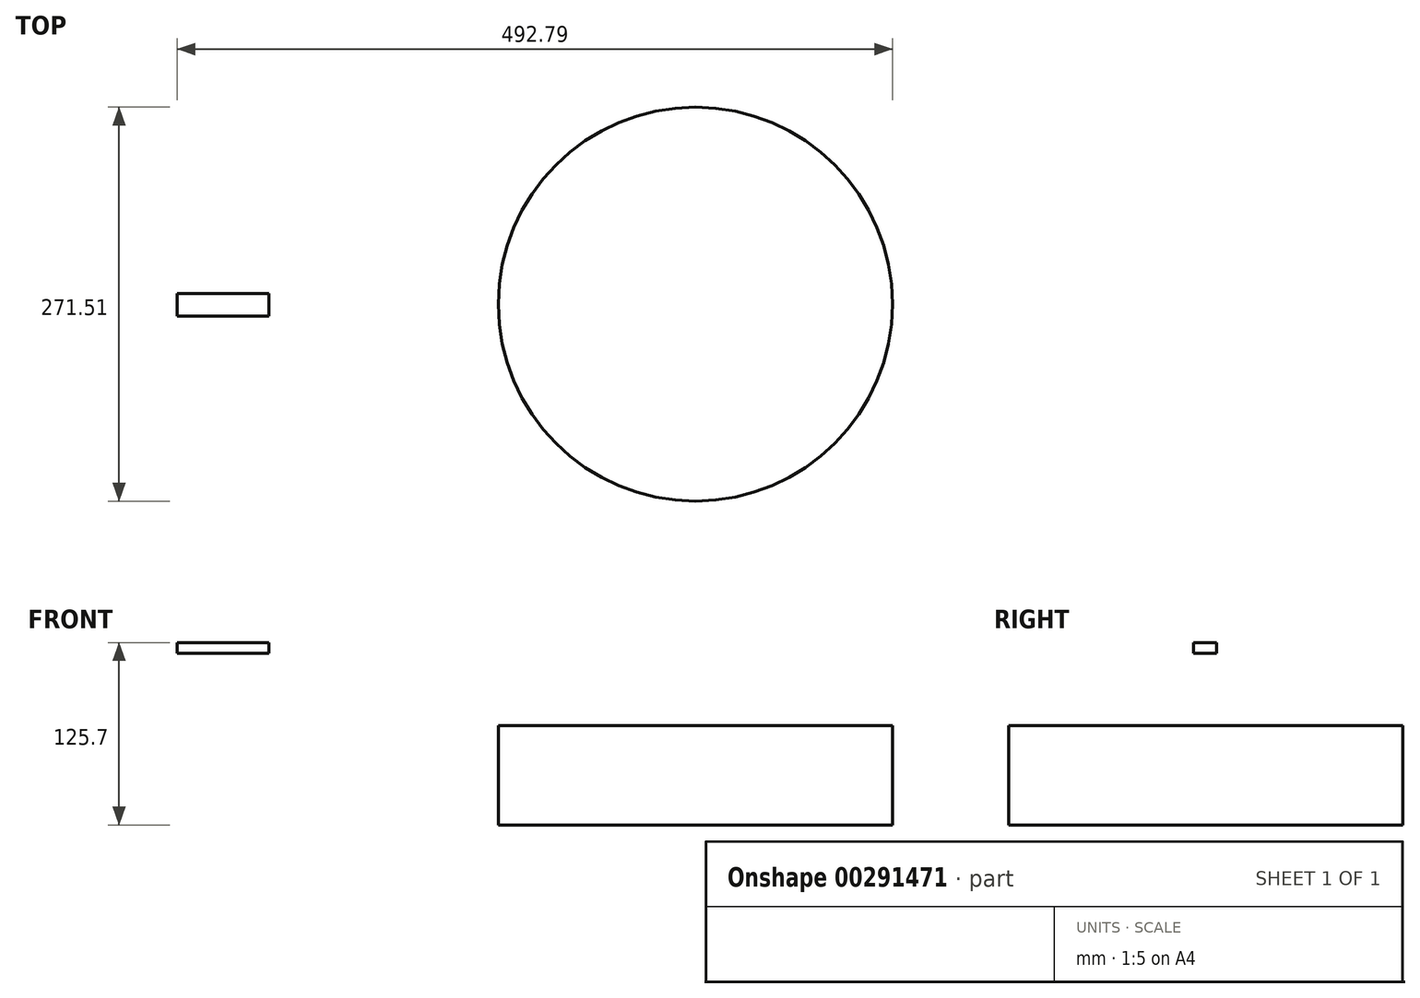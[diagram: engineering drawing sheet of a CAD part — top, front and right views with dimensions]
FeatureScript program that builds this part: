
annotation { "Feature Type Name" : "Feature", "Feature Type Description" : "" }
export const myFeature = defineFeature(function(context is Context, id is Id, definition is map)
    precondition{}
    {
        {
            var Q0;
            Q0=qCreatedBy(makeId("Front.planeOp"),FACE);
            var sketch = newSketch(context, id + "F0", { "sketchPlane" : qUnion([Q0])});
            skSolve(sketch);
        }
        {
            var Q0;
            Q0=qCreatedBy(makeId("Top.planeOp"),FACE);
            var sketch = newSketch(context, id + "F1", { "sketchPlane" : qUnion([Q0])});
            skCircle(sketch, "E0", {"center": v(0, 0) * mm, "radius": 8.39 * mm});
            skSolve(sketch);
        }
        {
            var Q0;
            Q0=makeQuery(id+"F1.imprint","IMPRINT",FACE,{"disambiguationData":[TD([[makeQuery(id+"F1.imprint","IMPRINT",EDGE,{"derivedFrom":sQuery(id+"F1.wireOp",EDGE,"E0")}),1.0]])]});
            var Q1;
            Q1=sQuery(id+"F1.wireOp",EDGE,"E0");
            var Q2;
            Q2 = qConstructionFilter(qBodyType(qCreatedBy(id + "F0" ,EDGE), BodyType.WIRE), ConstructionObject.NO);
            extrude(context, id + "F2", {"entities" : qUnion([Q0]), "bodyType" : ToolBodyType.SURFACE, "surfaceEntities" : qUnion([Q1, Q2]), "endBound" : BoundingType.SYMMETRIC, "depth" : 95 * mm, "offsetDistance" : 25.4 * mm});
        }
        {
            var Q0;
            Q0=qCreatedBy(makeId("Front.planeOp"),FACE);
            var sketch = newSketch(context, id + "F3", { "sketchPlane" : qUnion([Q0])});
            skLineSegment(sketch, "E1.bottom", {"start": v(-71.58, 57.12) * mm, "end": v(-8.49, 57.12) * mm});
            skLineSegment(sketch, "E1.top", {"start": v(-71.58, 49.67) * mm, "end": v(-8.49, 49.67) * mm});
            skLineSegment(sketch, "E1.left", {"start": v(-71.58, 57.12) * mm, "end": v(-71.58, 49.67) * mm});
            skLineSegment(sketch, "E1.right", {"start": v(-8.49, 57.12) * mm, "end": v(-8.49, 49.67) * mm});
            skSolve(sketch);
        }
        {
            var Q0;
            Q0=makeQuery(id+"F3.imprint","IMPRINT",FACE,{"disambiguationData":[TD([[makeQuery(id+"F3.imprint","IMPRINT",EDGE,{"derivedFrom":sQuery(id+"F3.wireOp",EDGE,"E1.bottom")}),-1.0]])]});
            extrude(context, id + "F4", {"entities" : qUnion([Q0]), "endBound" : BoundingType.SYMMETRIC, "depth" : 15.75 * mm, "offsetDistance" : 25.4 * mm});
        }
        {
            var Q0;
            Q0=qCreatedBy(makeId("Right.planeOp"),FACE);
            var sketch = newSketch(context, id + "F5", { "sketchPlane" : qUnion([Q0])});
            skCircle(sketch, "E2", {"center": v(0, 26.45) * mm, "radius": 7.62 * mm});
            skSolve(sketch);
        }
        {
            var Q0;
            Q0 = qSketchRegion(id + "F5", true);
            var Q1;
            Q1=sQuery(id+"F5.wireOp",EDGE,"E2");
            extrude(context, id + "F6", {"entities" : qUnion([Q0]), "bodyType" : ToolBodyType.SURFACE, "surfaceEntities" : qUnion([Q1]), "depth" : 149.1 * mm, "offsetDistance" : 25.4 * mm});
        }
        {
            var Q0;
            Q0=qCreatedBy(makeId("Top.planeOp"),FACE);
            var sketch = newSketch(context, id + "F7", { "sketchPlane" : qUnion([Q0])});
            skLineSegment(sketch, "E3", {"start": v(149.7, 0.42) * mm, "end": v(285.45, 0.42) * mm});
            skCircle(sketch, "E4", {"center": v(285.45, 0.42) * mm, "radius": 135.75 * mm});
            skSolve(sketch);
        }
        {
            var Q0;
            Q0=makeQuery(id+"F7.imprint","IMPRINT",FACE,{"disambiguationData":[TD([[makeQuery(id+"F7.imprint","IMPRINT",EDGE,{"derivedFrom":sQuery(id+"F7.wireOp",EDGE,"E4")}),1.0]])]});
            extrude(context, id + "F8", {"entities" : qUnion([Q0]), "oppositeDirection" : true, "depth" : 68.58 * mm, "offsetDistance" : 25.4 * mm});
        }
    });
